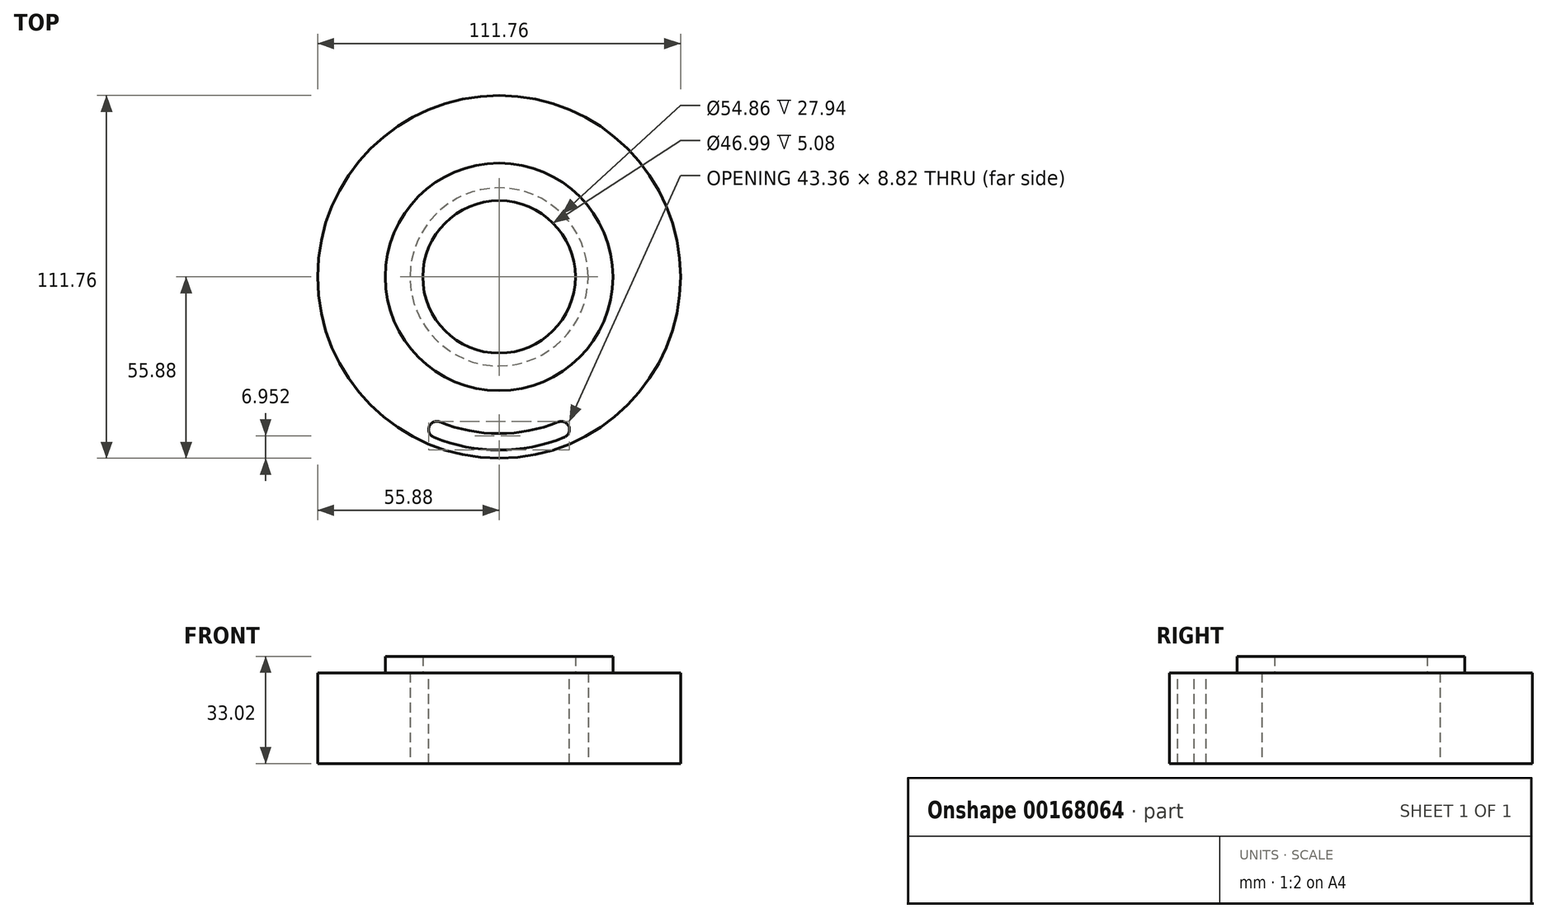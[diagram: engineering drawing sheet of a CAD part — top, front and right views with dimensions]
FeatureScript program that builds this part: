
annotation { "Feature Type Name" : "Feature", "Feature Type Description" : "" }
export const myFeature = defineFeature(function(context is Context, id is Id, definition is map)
    precondition{}
    {
        {
            var Q0;
            Q0=qCreatedBy(makeId("Top.planeOp"),FACE);
            var sketch = newSketch(context, id + "F0", { "sketchPlane" : qUnion([Q0])});
            skCircle(sketch, "E0", {"center": v(0, 0) * mm, "radius": 55.88 * mm});
            skCircle(sketch, "E1", {"center": v(0, 0) * mm, "radius": 27.43 * mm});
            skSolve(sketch);
        }
        {
            var Q0;
            Q0=qSketchRegion(id+"F0",true);
            extrude(context, id + "F1", {"entities" : qUnion([Q0]), "depth" : 27.94 * mm});
        }
        {
            var Q0;
            Q0=makeQuery(id+"F1.opExtrude","CAP_FACE",FACE,{"disambiguationData":[OSD([sQuery(id+"F0.wireOp",EDGE,"E0"),sQuery(id+"F0.wireOp",EDGE,"E1")])],"isStart":false});
            var sketch = newSketch(context, id + "F2", { "sketchPlane" : qUnion([Q0])});
            skCircle(sketch, "E2", {"center": v(0, 0) * mm, "radius": 35.05 * mm});
            skCircle(sketch, "E3", {"center": v(0, 0) * mm, "radius": 23.5 * mm});
            skSolve(sketch);
        }
        {
            var Q0;
            Q0=qSketchRegion(id+"F2",true);
            extrude(context, id + "F3", {"entities" : qUnion([Q0]), "operationType" : NewBodyOperationType.ADD, "depth" : 5.08 * mm});
        }
        {
            var Q0;
            Q0=makeQuery(id+"F1.opExtrude","CAP_FACE",FACE,{"disambiguationData":[OSD([sQuery(id+"F0.wireOp",EDGE,"E0"),sQuery(id+"F0.wireOp",EDGE,"E1")])],"isStart":false});
            var sketch = newSketch(context, id + "F4", { "sketchPlane" : qUnion([Q0])});
            skArc(sketch, "E4", {"start": v(21.47, -46.04) * mm, "mid": v(0, -50.8) * mm, "end": v(-21.47, -46.04) * mm, "construction": true});
            skLineSegment(sketch, "E5", {"start": v(-21.47, -46.04) * mm, "end": v(0, 0) * mm, "construction": true});
            skLineSegment(sketch, "E6", {"start": v(21.47, -46.04) * mm, "end": v(0, 0) * mm, "construction": true});
            skArc(sketch, "E7", {"start": v(-20.4, -43.74) * mm, "mid": v(0, -48.26) * mm, "end": v(20.4, -43.74) * mm});
            skArc(sketch, "E8", {"start": v(-22.54, -48.34) * mm, "mid": v(0, -53.34) * mm, "end": v(22.54, -48.34) * mm});
            skLineSegment(sketch, "E9", {"start": v(-22.54, -48.34) * mm, "end": v(-21.47, -46.04) * mm, "construction": true});
            skLineSegment(sketch, "E10", {"start": v(22.54, -48.34) * mm, "end": v(21.47, -46.04) * mm, "construction": true});
            skLineSegment(sketch, "E11", {"start": v(20.4, -43.74) * mm, "end": v(22.54, -48.34) * mm});
            skLineSegment(sketch, "E12", {"start": v(-22.54, -48.34) * mm, "end": v(-20.4, -43.74) * mm});
            skSolve(sketch);
        }
        {
            var Q0;
            Q0=qSketchRegion(id+"F4",true);
            extrude(context, id + "F5", {"entities" : qUnion([Q0]), "operationType" : NewBodyOperationType.REMOVE, "endBound" : BoundingType.THROUGH_ALL, "oppositeDirection" : true, "depth" : 25.4 * mm});
        }
        {
            var Q0;
            Q0=makeQuery(id+"F5.boolean.opBoolean","COPY",EDGE,{"derivedFrom":makeQuery(id+"F5.opExtrude","SWEPT_EDGE",EDGE,{"disambiguationData":[OSD([sQuery(id+"F4.wireOp",EDGE,"E8"),sQuery(id+"F4.wireOp",EDGE,"E12")])]})});
            var Q1;
            Q1=makeQuery(id+"F5.boolean.opBoolean","COPY",EDGE,{"derivedFrom":makeQuery(id+"F5.opExtrude","SWEPT_EDGE",EDGE,{"disambiguationData":[OSD([sQuery(id+"F4.wireOp",EDGE,"E7"),sQuery(id+"F4.wireOp",EDGE,"E12")])]})});
            var Q2;
            Q2=makeQuery(id+"F5.boolean.opBoolean","COPY",EDGE,{"derivedFrom":makeQuery(id+"F5.opExtrude","SWEPT_EDGE",EDGE,{"disambiguationData":[OSD([sQuery(id+"F4.wireOp",EDGE,"E8"),sQuery(id+"F4.wireOp",EDGE,"E11")])]})});
            var Q3;
            Q3=makeQuery(id+"F5.boolean.opBoolean","COPY",EDGE,{"derivedFrom":makeQuery(id+"F5.opExtrude","SWEPT_EDGE",EDGE,{"disambiguationData":[OSD([sQuery(id+"F4.wireOp",EDGE,"E7"),sQuery(id+"F4.wireOp",EDGE,"E11")])]})});
            fillet(context, id + "F6", {"entities" : qUnion([Q0, Q1, Q2, Q3]), "radius" : 2.54 * mm, "tangentPropagation" : true, "allowEdgeOverflow" : false});
        }
    });
